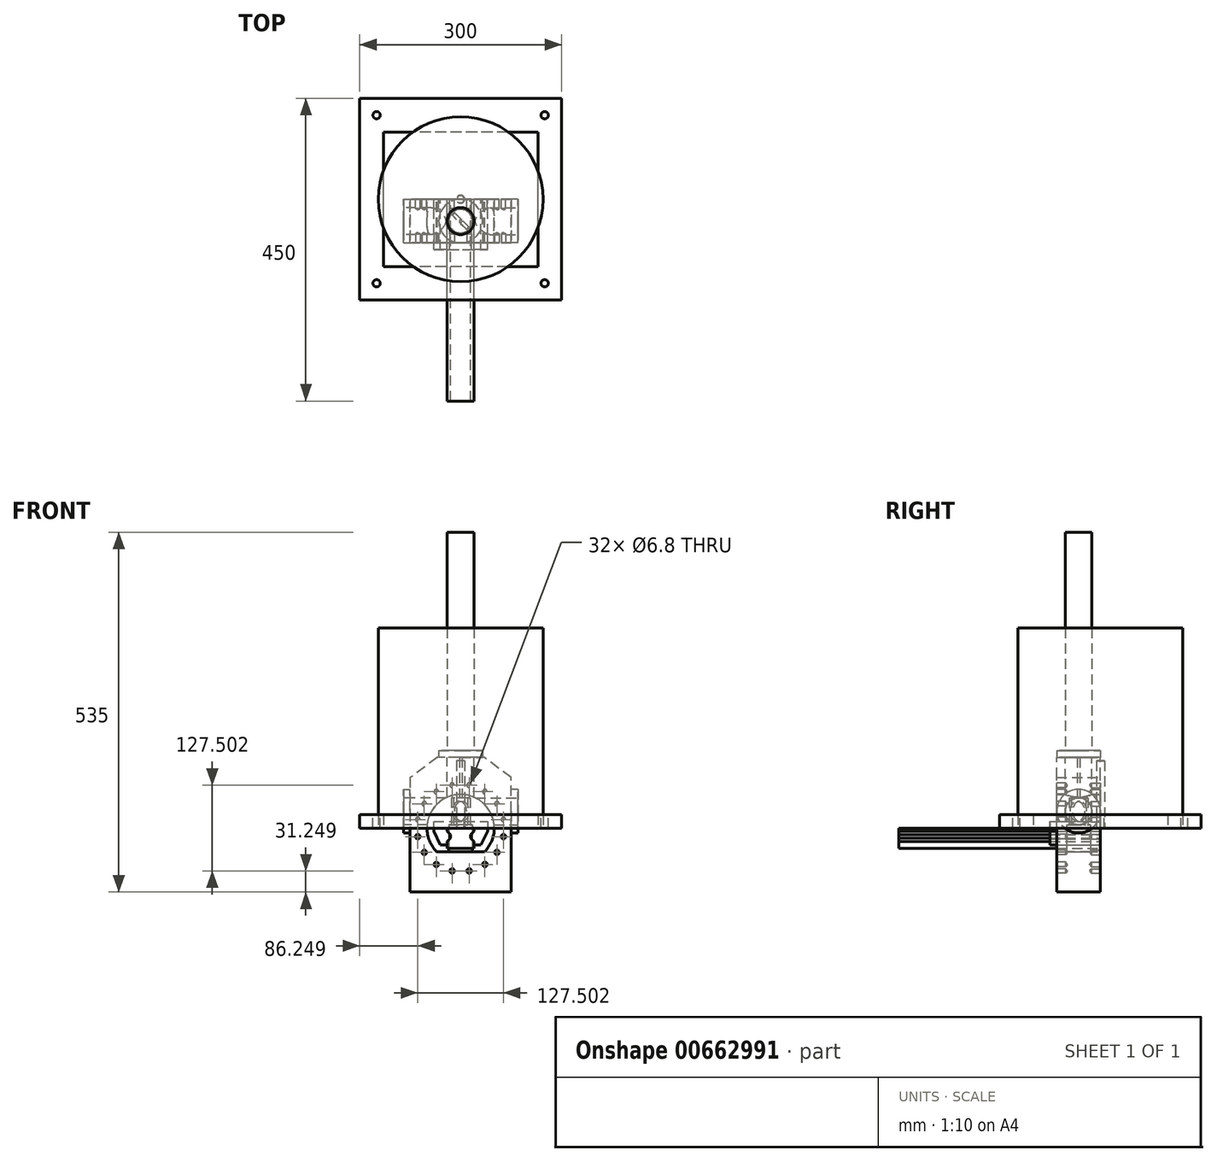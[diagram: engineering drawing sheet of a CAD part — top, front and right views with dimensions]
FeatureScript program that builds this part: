
annotation { "Feature Type Name" : "Feature", "Feature Type Description" : "" }
export const myFeature = defineFeature(function(context is Context, id is Id, definition is map)
    precondition{}
    {
        {
            var Q0;
            Q0=qCreatedBy(makeId("Front.planeOp"),FACE);
            var sketch = newSketch(context, id + "F0", { "sketchPlane" : qUnion([Q0])});
            skLineSegment(sketch, "E0", {"start": v(-75, -95) * mm, "end": v(75, -95) * mm});
            skLineSegment(sketch, "E1", {"start": v(75, -95) * mm, "end": v(75, 75) * mm});
            skLineSegment(sketch, "E2", {"start": v(75, 75) * mm, "end": v(35, 105) * mm});
            skLineSegment(sketch, "E3", {"start": v(35, 105) * mm, "end": v(-35, 105) * mm});
            skLineSegment(sketch, "E4", {"start": v(-35, 105) * mm, "end": v(-75, 75) * mm});
            skLineSegment(sketch, "E5", {"start": v(-75, 75) * mm, "end": v(-75, -95) * mm});
            skSolve(sketch);
        }
        {
            var Q0;
            Q0=makeQuery(id+"F0.imprint","IMPRINT",FACE,{"disambiguationData":[TD([[makeQuery(id+"F0.imprint","IMPRINT",EDGE,{"derivedFrom":sQuery(id+"F0.wireOp",EDGE,"E0")}),1.0]])]});
            extrude(context, id + "F1", {"entities" : qUnion([Q0]), "depth" : 65 * mm, "offsetDistance" : 25 * mm});
        }
        {
            var Q0;
            Q0=makeQuery(id+"F1.opExtrude","CAP_FACE",FACE,{"disambiguationData":[OSD([sQuery(id+"F0.wireOp",EDGE,"E0"),sQuery(id+"F0.wireOp",EDGE,"E1"),sQuery(id+"F0.wireOp",EDGE,"E2"),sQuery(id+"F0.wireOp",EDGE,"E3"),sQuery(id+"F0.wireOp",EDGE,"E4"),sQuery(id+"F0.wireOp",EDGE,"E5")])],"isStart":true});
            var sketch = newSketch(context, id + "F2", { "sketchPlane" : qUnion([Q0])});
            skArc(sketch, "E6", {"start": v(35.7, -35) * mm, "mid": v(0, 50) * mm, "end": v(-35.7, -35) * mm});
            skCircle(sketch, "E7", {"center": v(0, 0) * mm, "radius": 65 * mm, "construction": true});
            skLineSegment(sketch, "E8", {"start": v(-35.7, -35) * mm, "end": v(35.7, -35) * mm});
            skPoint(sketch, "E9", {"position": v(12.68, 63.75) * mm});
            skLineSegment(sketch, "E10", {"start": v(12.68, 63.75) * mm, "end": v(0, 0) * mm, "construction": true});
            skPoint(sketch, "E11.1.0", {"position": v(36.11, 54.05) * mm});
            skPoint(sketch, "E11.2.0", {"position": v(54.05, 36.11) * mm});
            skPoint(sketch, "E11.3.0", {"position": v(63.75, 12.68) * mm});
            skPoint(sketch, "E11.4.0", {"position": v(63.75, -12.68) * mm});
            skPoint(sketch, "E11.5.0", {"position": v(54.05, -36.11) * mm});
            skPoint(sketch, "E11.6.0", {"position": v(36.11, -54.05) * mm});
            skPoint(sketch, "E11.7.0", {"position": v(12.68, -63.75) * mm});
            skPoint(sketch, "E11.8.0", {"position": v(-12.68, -63.75) * mm});
            skPoint(sketch, "E11.9.0", {"position": v(-36.11, -54.05) * mm});
            skPoint(sketch, "E11.10.0", {"position": v(-54.05, -36.11) * mm});
            skPoint(sketch, "E11.11.0", {"position": v(-63.75, -12.68) * mm});
            skPoint(sketch, "E11.12.0", {"position": v(-63.75, 12.68) * mm});
            skPoint(sketch, "E11.13.0", {"position": v(-54.05, 36.11) * mm});
            skPoint(sketch, "E11.14.0", {"position": v(-36.11, 54.05) * mm});
            skPoint(sketch, "E11.15.0", {"position": v(-12.68, 63.75) * mm});
            skSolve(sketch);
        }
        {
            var Q0;
            Q0=makeQuery(id+"F2.imprint","IMPRINT",FACE,{"disambiguationData":[TD([[makeQuery(id+"F2.imprint","IMPRINT",EDGE,{"derivedFrom":sQuery(id+"F2.wireOp",EDGE,"E6")}),1.0]])]});
            extrude(context, id + "F3", {"entities" : qUnion([Q0]), "operationType" : NewBodyOperationType.REMOVE, "endBound" : BoundingType.THROUGH_ALL, "oppositeDirection" : true, "depth" : 25 * mm, "offsetDistance" : 25 * mm});
        }
        {
            var Q0;
            Q0=sQuery(id+"F2.wireOp",VERTEX,"E9");
            var Q1;
            Q1=sQuery(id+"F2.wireOp",VERTEX,"E11.1.0");
            var Q2;
            Q2=sQuery(id+"F2.wireOp",VERTEX,"E11.2.0");
            var Q3;
            Q3=sQuery(id+"F2.wireOp",VERTEX,"E11.3.0");
            var Q4;
            Q4=sQuery(id+"F2.wireOp",VERTEX,"E11.4.0");
            var Q5;
            Q5=sQuery(id+"F2.wireOp",VERTEX,"E11.5.0");
            var Q6;
            Q6=sQuery(id+"F2.wireOp",VERTEX,"E11.6.0");
            var Q7;
            Q7=sQuery(id+"F2.wireOp",VERTEX,"E11.7.0");
            var Q8;
            Q8=sQuery(id+"F2.wireOp",VERTEX,"E11.8.0");
            var Q9;
            Q9=sQuery(id+"F2.wireOp",VERTEX,"E11.9.0");
            var Q10;
            Q10=sQuery(id+"F2.wireOp",VERTEX,"E11.10.0");
            var Q11;
            Q11=sQuery(id+"F2.wireOp",VERTEX,"E11.11.0");
            var Q12;
            Q12=sQuery(id+"F2.wireOp",VERTEX,"E11.12.0");
            var Q13;
            Q13=sQuery(id+"F2.wireOp",VERTEX,"E11.13.0");
            var Q14;
            Q14=sQuery(id+"F2.wireOp",VERTEX,"E11.14.0");
            var Q15;
            Q15=sQuery(id+"F2.wireOp",VERTEX,"E11.15.0");
            var Q16;
            Q16=makeQuery(id+"F1.opExtrude","SWEPT_BODY",BODY,{"disambiguationData":[OSD([sQuery(id+"F0.wireOp",EDGE,"E0"),sQuery(id+"F0.wireOp",EDGE,"E1"),sQuery(id+"F0.wireOp",EDGE,"E2"),sQuery(id+"F0.wireOp",EDGE,"E3"),sQuery(id+"F0.wireOp",EDGE,"E4"),sQuery(id+"F0.wireOp",EDGE,"E5")])]});
            hole(context, id + "F4", {"style" : HoleStyle.SIMPLE, "endStyle" : HoleEndStyle.BLIND, "standardTappedOrClearance" : lookupTablePath({ "standard" : "ISO", "engagement" : "75%", "pitch" : "1.25 mm", "size" : "M8", "type" : "Tapped" }), "standardBlindInLast" : lookupTablePath({ "standard" : "ISO", "fit" : "Normal", "engagement" : "75%", "pitch" : "1.25 mm", "size" : "M8", "type" : "Clearance & tapped" }), "holeDiameter" : 6.8 * mm, "majorDiameter" : 8 * mm, "showTappedDepth" : true, "holeDepth" : 13.75 * mm, "isTappedThrough" : true, "tappedDepth" : 10 * mm, "tapClearance" : 3, "locations" : qUnion([Q0, Q1, Q2, Q3, Q4, Q5, Q6, Q7, Q8, Q9, Q10, Q11, Q12, Q13, Q14, Q15]), "scope" : qUnion([Q16])});
        }
        {
            var Q0;
            Q0=makeQuery(id+"F1.opExtrude","SWEPT_FACE",FACE,{"disambiguationData":[OSD([sQuery(id+"F0.wireOp",EDGE,"E3")])]});
            var sketch = newSketch(context, id + "F5", { "sketchPlane" : qUnion([Q0])});
            skCircle(sketch, "E12", {"center": v(0, -32.5) * mm, "radius": 32.5 * mm});
            skPoint(sketch, "E12.centerSnap0", {"position": v(0, -65) * mm});
            skPoint(sketch, "E12.centerSnap1", {"position": v(35, -32.5) * mm});
            skCircle(sketch, "E13", {"center": v(0, -32.5) * mm, "radius": 20 * mm});
            skSolve(sketch);
        }
        {
            var Q0;
            Q0=makeQuery(id+"F5.imprint","IMPRINT",FACE,{"disambiguationData":[TD([[makeQuery(id+"F5.imprint","IMPRINT",EDGE,{"derivedFrom":sQuery(id+"F5.wireOp",EDGE,"E13")}),-1.0]])]});
            var Q1;
            Q1=makeQuery(id+"F5.imprint","IMPRINT",FACE,{"disambiguationData":[TD([[makeQuery(id+"F5.imprint","IMPRINT",EDGE,{"derivedFrom":sQuery(id+"F5.wireOp",EDGE,"E13")}),1.0]])]});
            extrude(context, id + "F6", {"entities" : qUnion([Q0, Q1]), "operationType" : NewBodyOperationType.ADD, "depth" : 10 * mm, "offsetDistance" : 25 * mm});
        }
        {
            var Q0;
            Q0=makeQuery(id+"F5.imprint","IMPRINT",FACE,{"disambiguationData":[TD([[makeQuery(id+"F5.imprint","IMPRINT",EDGE,{"derivedFrom":sQuery(id+"F5.wireOp",EDGE,"E13")}),1.0]])]});
            var Q1;
            Q1=makeQuery(id+"F3.boolean.opBoolean","COPY",FACE,{"derivedFrom":makeQuery(id+"F3.opExtrude","SWEPT_FACE",FACE,{"disambiguationData":[OSD([sQuery(id+"F2.wireOp",EDGE,"E6")])]})});
            extrude(context, id + "F7", {"entities" : qUnion([Q0]), "operationType" : NewBodyOperationType.REMOVE, "endBound" : BoundingType.UP_TO_SURFACE, "oppositeDirection" : true, "depth" : 25 * mm, "endBoundEntityFace" : qUnion([Q1]), "offsetDistance" : 25 * mm});
        }
        {
            var Q0;
            Q0=makeQuery(id+"F6.opExtrude","CAP_FACE",FACE,{"disambiguationData":[OSD([sQuery(id+"F5.wireOp",EDGE,"E12")])],"isStart":false});
            var sketch = newSketch(context, id + "F8", { "sketchPlane" : qUnion([Q0])});
            skCircle(sketch, "E14", {"center": v(0, -32.5) * mm, "radius": 20 * mm});
            skSolve(sketch);
        }
        {
            var Q0;
            Q0=makeQuery(id+"F8.imprint","IMPRINT",FACE,{"disambiguationData":[TD([[makeQuery(id+"F8.imprint","IMPRINT",EDGE,{"derivedFrom":sQuery(id+"F8.wireOp",EDGE,"E14")}),1.0]])]});
            extrude(context, id + "F9", {"entities" : qUnion([Q0]), "operationType" : NewBodyOperationType.ADD, "depth" : 325 * mm, "offsetDistance" : 25 * mm});
        }
        {
            var Q0;
            Q0=makeQuery(id+"F1.opExtrude","CAP_FACE",FACE,{"disambiguationData":[OSD([sQuery(id+"F0.wireOp",EDGE,"E0"),sQuery(id+"F0.wireOp",EDGE,"E1"),sQuery(id+"F0.wireOp",EDGE,"E2"),sQuery(id+"F0.wireOp",EDGE,"E3"),sQuery(id+"F0.wireOp",EDGE,"E4"),sQuery(id+"F0.wireOp",EDGE,"E5")])],"isStart":false});
            var sketch = newSketch(context, id + "F10", { "sketchPlane" : qUnion([Q0])});
            skCircle(sketch, "E15", {"center": v(0, 0) * mm, "radius": 65 * mm, "construction": true});
            skPoint(sketch, "E16", {"position": v(12.68, 63.75) * mm});
            skLineSegment(sketch, "E17", {"start": v(12.68, 63.75) * mm, "end": v(0, 0) * mm, "construction": true});
            skPoint(sketch, "E18.1.0", {"position": v(-12.68, 63.75) * mm});
            skPoint(sketch, "E18.2.0", {"position": v(-36.11, 54.05) * mm});
            skPoint(sketch, "E18.3.0", {"position": v(-54.05, 36.11) * mm});
            skPoint(sketch, "E18.4.0", {"position": v(-63.75, 12.68) * mm});
            skPoint(sketch, "E18.5.0", {"position": v(-63.75, -12.68) * mm});
            skPoint(sketch, "E18.6.0", {"position": v(-54.05, -36.11) * mm});
            skPoint(sketch, "E18.7.0", {"position": v(-36.11, -54.05) * mm});
            skPoint(sketch, "E18.8.0", {"position": v(-12.68, -63.75) * mm});
            skPoint(sketch, "E18.9.0", {"position": v(12.68, -63.75) * mm});
            skPoint(sketch, "E18.10.0", {"position": v(36.11, -54.05) * mm});
            skPoint(sketch, "E18.11.0", {"position": v(54.05, -36.11) * mm});
            skPoint(sketch, "E18.12.0", {"position": v(63.75, -12.68) * mm});
            skPoint(sketch, "E18.13.0", {"position": v(63.75, 12.68) * mm});
            skPoint(sketch, "E18.14.0", {"position": v(54.05, 36.11) * mm});
            skPoint(sketch, "E18.15.0", {"position": v(36.11, 54.05) * mm});
            skSolve(sketch);
        }
        {
            var Q0;
            Q0=sQuery(id+"F10.wireOp",VERTEX,"E16");
            var Q1;
            Q1=sQuery(id+"F10.wireOp",VERTEX,"E18.15.0");
            var Q2;
            Q2=sQuery(id+"F10.wireOp",VERTEX,"E18.14.0");
            var Q3;
            Q3=sQuery(id+"F10.wireOp",VERTEX,"E18.13.0");
            var Q4;
            Q4=sQuery(id+"F10.wireOp",VERTEX,"E18.12.0");
            var Q5;
            Q5=sQuery(id+"F10.wireOp",VERTEX,"E18.11.0");
            var Q6;
            Q6=sQuery(id+"F10.wireOp",VERTEX,"E18.10.0");
            var Q7;
            Q7=sQuery(id+"F10.wireOp",VERTEX,"E18.9.0");
            var Q8;
            Q8=sQuery(id+"F10.wireOp",VERTEX,"E18.8.0");
            var Q9;
            Q9=sQuery(id+"F10.wireOp",VERTEX,"E18.7.0");
            var Q10;
            Q10=sQuery(id+"F10.wireOp",VERTEX,"E18.6.0");
            var Q11;
            Q11=sQuery(id+"F10.wireOp",VERTEX,"E18.5.0");
            var Q12;
            Q12=sQuery(id+"F10.wireOp",VERTEX,"E18.4.0");
            var Q13;
            Q13=sQuery(id+"F10.wireOp",VERTEX,"E18.3.0");
            var Q14;
            Q14=sQuery(id+"F10.wireOp",VERTEX,"E18.2.0");
            var Q15;
            Q15=sQuery(id+"F10.wireOp",VERTEX,"E18.1.0");
            var Q16;
            Q16=makeQuery(id+"F1.opExtrude","SWEPT_BODY",BODY,{"disambiguationData":[OSD([sQuery(id+"F0.wireOp",EDGE,"E0"),sQuery(id+"F0.wireOp",EDGE,"E1"),sQuery(id+"F0.wireOp",EDGE,"E2"),sQuery(id+"F0.wireOp",EDGE,"E3"),sQuery(id+"F0.wireOp",EDGE,"E4"),sQuery(id+"F0.wireOp",EDGE,"E5")])]});
            hole(context, id + "F11", {"style" : HoleStyle.SIMPLE, "endStyle" : HoleEndStyle.BLIND, "standardTappedOrClearance" : lookupTablePath({ "standard" : "ISO", "engagement" : "75%", "pitch" : "1.25 mm", "size" : "M8", "type" : "Tapped" }), "standardBlindInLast" : lookupTablePath({ "fit" : "Normal", "standard" : "ISO", "engagement" : "75%", "pitch" : "1.25 mm", "size" : "M8", "type" : "Clearance & tapped" }), "holeDiameter" : 6.8 * mm, "majorDiameter" : 8 * mm, "showTappedDepth" : true, "holeDepth" : 13.75 * mm, "isTappedThrough" : true, "tappedDepth" : 10 * mm, "tapClearance" : 3, "locations" : qUnion([Q0, Q1, Q2, Q3, Q4, Q5, Q6, Q7, Q8, Q9, Q10, Q11, Q12, Q13, Q14, Q15]), "scope" : qUnion([Q16])});
        }
        {
            var Q0;
            Q0=makeQuery(id+"F1.opExtrude","SWEPT_FACE",FACE,{"disambiguationData":[OSD([sQuery(id+"F0.wireOp",EDGE,"E5")])]});
            var sketch = newSketch(context, id + "F12", { "sketchPlane" : qUnion([Q0])});
            skCircle(sketch, "E19", {"center": v(32.5, 25) * mm, "radius": 20 * mm});
            skPoint(sketch, "E19.centerSnap0", {"position": v(32.5, 75) * mm});
            skCircle(sketch, "E20", {"center": v(32.5, 25) * mm, "radius": 32.5 * mm});
            skSolve(sketch);
        }
        {
            var Q0;
            Q0=makeQuery(id+"F12.imprint","IMPRINT",FACE,{"disambiguationData":[TD([[makeQuery(id+"F12.imprint","IMPRINT",EDGE,{"derivedFrom":sQuery(id+"F12.wireOp",EDGE,"E19")}),1.0]])]});
            var Q1;
            Q1=makeQuery(id+"F3.boolean.opBoolean","COPY",FACE,{"derivedFrom":makeQuery(id+"F3.opExtrude","SWEPT_FACE",FACE,{"disambiguationData":[OSD([sQuery(id+"F2.wireOp",EDGE,"E6")])]})});
            extrude(context, id + "F13", {"entities" : qUnion([Q0]), "operationType" : NewBodyOperationType.REMOVE, "endBound" : BoundingType.UP_TO_SURFACE, "oppositeDirection" : true, "depth" : 25 * mm, "endBoundEntityFace" : qUnion([Q1]), "offsetDistance" : 25 * mm});
        }
        {
            var Q0;
            Q0=makeQuery(id+"F12.imprint","IMPRINT",FACE,{"disambiguationData":[TD([[makeQuery(id+"F12.imprint","IMPRINT",EDGE,{"derivedFrom":sQuery(id+"F12.wireOp",EDGE,"E19")}),-1.0]])]});
            extrude(context, id + "F14", {"entities" : qUnion([Q0]), "operationType" : NewBodyOperationType.ADD, "depth" : 10 * mm, "offsetDistance" : 25 * mm});
        }
        {
            var Q0;
            Q0=makeQuery(id+"F1.opExtrude","SWEPT_FACE",FACE,{"disambiguationData":[OSD([sQuery(id+"F0.wireOp",EDGE,"E1")])]});
            var sketch = newSketch(context, id + "F15", { "sketchPlane" : qUnion([Q0])});
            skCircle(sketch, "E21", {"center": v(-32.5, 25) * mm, "radius": 20 * mm});
            skPoint(sketch, "E21.centerSnap0", {"position": v(-32.5, 75) * mm});
            skCircle(sketch, "E22", {"center": v(-32.5, 25) * mm, "radius": 32.5 * mm});
            skSolve(sketch);
        }
        {
            var Q0;
            Q0=makeQuery(id+"F15.imprint","IMPRINT",FACE,{"disambiguationData":[TD([[makeQuery(id+"F15.imprint","IMPRINT",EDGE,{"derivedFrom":sQuery(id+"F15.wireOp",EDGE,"E21")}),1.0]])]});
            var Q1;
            Q1=makeQuery(id+"F3.boolean.opBoolean","COPY",FACE,{"derivedFrom":makeQuery(id+"F3.opExtrude","SWEPT_FACE",FACE,{"disambiguationData":[OSD([sQuery(id+"F2.wireOp",EDGE,"E6")])]})});
            extrude(context, id + "F16", {"entities" : qUnion([Q0]), "operationType" : NewBodyOperationType.REMOVE, "endBound" : BoundingType.UP_TO_SURFACE, "oppositeDirection" : true, "depth" : 25 * mm, "endBoundEntityFace" : qUnion([Q1]), "offsetDistance" : 25 * mm});
        }
        {
            var Q0;
            Q0=makeQuery(id+"F15.imprint","IMPRINT",FACE,{"disambiguationData":[TD([[makeQuery(id+"F15.imprint","IMPRINT",EDGE,{"derivedFrom":sQuery(id+"F15.wireOp",EDGE,"E21")}),-1.0]])]});
            extrude(context, id + "F17", {"entities" : qUnion([Q0]), "operationType" : NewBodyOperationType.ADD, "depth" : 10 * mm, "offsetDistance" : 25 * mm});
        }
        {
            var Q0;
            Q0=makeQuery(id+"F3.boolean.opBoolean","COPY",FACE,{"derivedFrom":makeQuery(id+"F3.opExtrude","SWEPT_FACE",FACE,{"disambiguationData":[OSD([sQuery(id+"F2.wireOp",EDGE,"E8")])]})});
            var sketch = newSketch(context, id + "F18", { "sketchPlane" : qUnion([Q0])});
            skCircle(sketch, "E23", {"center": v(0, -32.5) * mm, "radius": 17.5 * mm});
            skPoint(sketch, "E23.centerSnap0", {"position": v(35.7, -32.5) * mm});
            skSolve(sketch);
        }
        {
            var Q0;
            Q0=makeQuery(id+"F18.imprint","IMPRINT",FACE,{"disambiguationData":[TD([[makeQuery(id+"F18.imprint","IMPRINT",EDGE,{"derivedFrom":sQuery(id+"F18.wireOp",EDGE,"E23")}),1.0]])]});
            extrude(context, id + "F19", {"entities" : qUnion([Q0]), "operationType" : NewBodyOperationType.ADD, "depth" : 40 * mm, "offsetDistance" : 25 * mm});
        }
        {
            var Q0;
            Q0=makeQuery(id+"F19.opExtrude","CAP_FACE",FACE,{"disambiguationData":[OSD([sQuery(id+"F18.wireOp",EDGE,"E23")])],"isStart":false});
            var sketch = newSketch(context, id + "F20", { "sketchPlane" : qUnion([Q0])});
            skLineSegment(sketch, "E24", {"start": v(14.02, -42.98) * mm, "end": v(-10.48, -18.48) * mm});
            skLineSegment(sketch, "E25", {"start": v(0, -32.5) * mm, "end": v(12.37, -44.87) * mm, "construction": true});
            skLineSegment(sketch, "E26", {"start": v(10.48, -46.52) * mm, "end": v(-14.02, -22.02) * mm});
            skSolve(sketch);
        }
        {
            var Q0;
            {var subQ0=sQuery(id+"F20.wireOp",EDGE,"E24");Q0=makeQuery(id+"F20.imprint","IMPRINT",FACE,{"disambiguationData":[TD([[makeQuery(id+"F20.imprint","IMPRINT",EDGE,{"derivedFrom":subQ0}),1.0]])]});}
            extrude(context, id + "F21", {"entities" : qUnion([Q0]), "operationType" : NewBodyOperationType.ADD, "depth" : 40 * mm, "offsetDistance" : 25 * mm});
        }
        {
            var Q0;
            Q0=makeQuery(id+"F21.opExtrude","SWEPT_FACE",FACE,{"disambiguationData":[OSD([sQuery(id+"F20.wireOp",EDGE,"E24")])]});
            var sketch = newSketch(context, id + "F22", { "sketchPlane" : qUnion([Q0])});
            skCircle(sketch, "E27", {"center": v(-22.98, 25) * mm, "radius": 15 * mm});
            skPoint(sketch, "E27.centerSnap0", {"position": v(-22.98, 45) * mm});
            skSolve(sketch);
        }
        {
            var Q0;
            Q0=makeQuery(id+"F22.imprint","IMPRINT",FACE,{"disambiguationData":[TD([[makeQuery(id+"F22.imprint","IMPRINT",EDGE,{"derivedFrom":sQuery(id+"F22.wireOp",EDGE,"E27")}),1.0]])]});
            var Q1;
            Q1=makeQuery(id+"F21.opExtrude","SWEPT_FACE",FACE,{"disambiguationData":[OSD([sQuery(id+"F20.wireOp",EDGE,"E26")])]});
            extrude(context, id + "F23", {"entities" : qUnion([Q0]), "operationType" : NewBodyOperationType.REMOVE, "endBound" : BoundingType.UP_TO_SURFACE, "oppositeDirection" : true, "depth" : 25 * mm, "endBoundEntityFace" : qUnion([Q1]), "offsetDistance" : 25 * mm});
        }
        {
            var Q0;
            Q0=makeQuery(id+"F21.opExtrude","CAP_FACE",FACE,{"disambiguationData":[OSD([sQuery(id+"F18.wireOp",EDGE,"E23"),sQuery(id+"F20.wireOp",EDGE,"E24"),sQuery(id+"F20.wireOp",EDGE,"E26")])],"isStart":false});
            var sketch = newSketch(context, id + "F24", { "sketchPlane" : qUnion([Q0])});
            skCircle(sketch, "E28", {"center": v(0, -32.5) * mm, "radius": 2 * mm});
            skSolve(sketch);
        }
        {
            var Q0;
            Q0=makeQuery(id+"F24.imprint","IMPRINT",FACE,{"disambiguationData":[TD([[makeQuery(id+"F24.imprint","IMPRINT",EDGE,{"derivedFrom":sQuery(id+"F24.wireOp",EDGE,"E28")}),1.0]])]});
            extrude(context, id + "F25", {"entities" : qUnion([Q0]), "operationType" : NewBodyOperationType.ADD, "endBound" : BoundingType.UP_TO_NEXT, "depth" : 25 * mm, "offsetDistance" : 25 * mm});
        }
        {
            var Q0;
            Q0=qCreatedBy(makeId("Top.planeOp"),FACE);
            var sketch = newSketch(context, id + "F26", { "sketchPlane" : qUnion([Q0])});
            skLineSegment(sketch, "E29.bottom", {"start": v(-150, 150) * mm, "end": v(150, 150) * mm});
            skLineSegment(sketch, "E29.top", {"start": v(-150, -150) * mm, "end": v(150, -150) * mm});
            skLineSegment(sketch, "E29.left", {"start": v(-150, 150) * mm, "end": v(-150, -150) * mm});
            skLineSegment(sketch, "E29.right", {"start": v(150, 150) * mm, "end": v(150, -150) * mm});
            skPoint(sketch, "E29.middle", {"position": v(0, 0) * mm});
            skSolve(sketch);
        }
        {
            var Q0;
            Q0=makeQuery(id+"F26.imprint","IMPRINT",FACE,{"disambiguationData":[TD([[makeQuery(id+"F26.imprint","IMPRINT",EDGE,{"derivedFrom":sQuery(id+"F26.wireOp",EDGE,"E29.bottom")}),-1.0]])]});
            extrude(context, id + "F27", {"entities" : qUnion([Q0]), "depth" : 20 * mm, "offsetDistance" : 25 * mm});
        }
        {
            var Q0;
            Q0=makeQuery(id+"F27.opExtrude","CAP_FACE",FACE,{"disambiguationData":[OSD([sQuery(id+"F26.wireOp",EDGE,"E29.bottom"),sQuery(id+"F26.wireOp",EDGE,"E29.top"),sQuery(id+"F26.wireOp",EDGE,"E29.left"),sQuery(id+"F26.wireOp",EDGE,"E29.right")])],"isStart":false});
            var sketch = newSketch(context, id + "F28", { "sketchPlane" : qUnion([Q0])});
            skCircle(sketch, "E30", {"center": v(0, 0) * mm, "radius": 122.5 * mm, "construction": true});
            skLineSegment(sketch, "E31.bottom", {"start": v(-125, -125) * mm, "end": v(125, -125) * mm, "construction": true});
            skLineSegment(sketch, "E31.top", {"start": v(-125, 125) * mm, "end": v(125, 125) * mm, "construction": true});
            skLineSegment(sketch, "E31.left", {"start": v(-125, -125) * mm, "end": v(-125, 125) * mm, "construction": true});
            skLineSegment(sketch, "E31.right", {"start": v(125, -125) * mm, "end": v(125, 125) * mm, "construction": true});
            skSolve(sketch);
        }
        {
            var Q0;
            Q0=sQuery(id+"F28.wireOp",VERTEX,"E31.bottom.end");
            var Q1;
            Q1=sQuery(id+"F28.wireOp",VERTEX,"E31.top.end");
            var Q2;
            Q2=sQuery(id+"F28.wireOp",VERTEX,"E31.top.start");
            var Q3;
            Q3=sQuery(id+"F28.wireOp",VERTEX,"E31.bottom.start");
            var Q4;
            Q4=sQuery(id+"F28.wireOp",VERTEX,"E30.center");
            var Q5;
            Q5=makeQuery(id+"F27.opExtrude","SWEPT_BODY",BODY,{"disambiguationData":[OSD([sQuery(id+"F26.wireOp",EDGE,"E29.bottom"),sQuery(id+"F26.wireOp",EDGE,"E29.top"),sQuery(id+"F26.wireOp",EDGE,"E29.left"),sQuery(id+"F26.wireOp",EDGE,"E29.right")])]});
            hole(context, id + "F29", {"style" : HoleStyle.SIMPLE, "endStyle" : HoleEndStyle.THROUGH, "standardTappedOrClearance" : lookupTablePath({ "standard" : "ISO", "engagement" : "75%", "pitch" : "1.25 mm", "size" : "M12", "type" : "Tapped" }), "standardBlindInLast" : lookupTablePath({ "standard" : "ISO", "fit" : "Normal", "engagement" : "75%", "pitch" : "1.25 mm", "size" : "M12", "type" : "Clearance & tapped" }), "holeDiameter" : 10.8 * mm, "majorDiameter" : 12 * mm, "showTappedDepth" : true, "isTappedThrough" : true, "tappedDepth" : 10 * mm, "tapClearance" : 3, "locations" : qUnion([Q0, Q1, Q2, Q3, Q4]), "scope" : qUnion([Q5])});
        }
        {
            var Q0;
            Q0=qCreatedBy(makeId("Top.planeOp"),FACE);
            var sketch = newSketch(context, id + "F30", { "sketchPlane" : qUnion([Q0])});
            skLineSegment(sketch, "E32.bottom", {"start": v(-150, -150) * mm, "end": v(150, -150) * mm});
            skLineSegment(sketch, "E32.top", {"start": v(-150, 150) * mm, "end": v(150, 150) * mm});
            skLineSegment(sketch, "E32.left", {"start": v(-150, -150) * mm, "end": v(-150, 150) * mm});
            skLineSegment(sketch, "E32.right", {"start": v(150, -150) * mm, "end": v(150, 150) * mm});
            skPoint(sketch, "E32.middle", {"position": v(0, 0) * mm});
            skSolve(sketch);
        }
        {
            var Q0;
            Q0=makeQuery(id+"F30.imprint","IMPRINT",FACE,{"disambiguationData":[TD([[makeQuery(id+"F30.imprint","IMPRINT",EDGE,{"derivedFrom":sQuery(id+"F30.wireOp",EDGE,"E32.bottom")}),1.0]])]});
            extrude(context, id + "F31", {"entities" : qUnion([Q0]), "depth" : 20 * mm, "offsetDistance" : 25 * mm});
        }
        {
            var Q0;
            Q0=makeQuery(id+"F31.opExtrude","CAP_FACE",FACE,{"disambiguationData":[OSD([sQuery(id+"F30.wireOp",EDGE,"E32.bottom"),sQuery(id+"F30.wireOp",EDGE,"E32.top"),sQuery(id+"F30.wireOp",EDGE,"E32.left"),sQuery(id+"F30.wireOp",EDGE,"E32.right")])],"isStart":false});
            var sketch = newSketch(context, id + "F32", { "sketchPlane" : qUnion([Q0])});
            skLineSegment(sketch, "E33.bottom", {"start": v(125, -125) * mm, "end": v(-125, -125) * mm, "construction": true});
            skLineSegment(sketch, "E33.top", {"start": v(125, 125) * mm, "end": v(-125, 125) * mm, "construction": true});
            skLineSegment(sketch, "E33.left", {"start": v(125, -125) * mm, "end": v(125, 125) * mm, "construction": true});
            skLineSegment(sketch, "E33.right", {"start": v(-125, -125) * mm, "end": v(-125, 125) * mm, "construction": true});
            skPoint(sketch, "E33.middle", {"position": v(0, 0) * mm});
            skSolve(sketch);
        }
        {
            var Q0;
            Q0=sQuery(id+"F32.wireOp",VERTEX,"E33.middle");
            var Q1;
            Q1=sQuery(id+"F32.wireOp",VERTEX,"E33.top.end");
            var Q2;
            Q2=sQuery(id+"F32.wireOp",VERTEX,"E33.bottom.end");
            var Q3;
            Q3=sQuery(id+"F32.wireOp",VERTEX,"E33.bottom.start");
            var Q4;
            Q4=sQuery(id+"F32.wireOp",VERTEX,"E33.top.start");
            var Q5;
            Q5=makeQuery(id+"F31.opExtrude","SWEPT_BODY",BODY,{"disambiguationData":[OSD([sQuery(id+"F30.wireOp",EDGE,"E32.bottom"),sQuery(id+"F30.wireOp",EDGE,"E32.top"),sQuery(id+"F30.wireOp",EDGE,"E32.left"),sQuery(id+"F30.wireOp",EDGE,"E32.right")])]});
            hole(context, id + "F33", {"style" : HoleStyle.SIMPLE, "endStyle" : HoleEndStyle.THROUGH, "standardTappedOrClearance" : lookupTablePath({ "standard" : "ISO", "engagement" : "75%", "pitch" : "1.25 mm", "size" : "M12", "type" : "Tapped" }), "standardBlindInLast" : lookupTablePath({ "fit" : "Normal", "standard" : "ISO", "engagement" : "75%", "pitch" : "1.25 mm", "size" : "M12", "type" : "Clearance & tapped" }), "holeDiameter" : 10.8 * mm, "majorDiameter" : 12 * mm, "showTappedDepth" : true, "isTappedThrough" : true, "tappedDepth" : 10 * mm, "tapClearance" : 3, "locations" : qUnion([Q0, Q1, Q2, Q3, Q4]), "scope" : qUnion([Q5])});
        }
        {
            var Q0;
            Q0=qCreatedBy(makeId("Front.planeOp"),FACE);
            var sketch = newSketch(context, id + "F34", { "sketchPlane" : qUnion([Q0])});
            skLineSegment(sketch, "E34", {"start": v(0, -30) * mm, "end": v(-20, -30) * mm});
            skLineSegment(sketch, "E35", {"start": v(-20, -30) * mm, "end": v(-20, -20) * mm});
            skLineSegment(sketch, "E36", {"start": v(-20, -20) * mm, "end": v(-15, -15) * mm});
            skLineSegment(sketch, "E37", {"start": v(-15, -15) * mm, "end": v(-15, -10) * mm});
            skLineSegment(sketch, "E38", {"start": v(-15, -10) * mm, "end": v(-20, -5) * mm});
            skLineSegment(sketch, "E39", {"start": v(-20, -5) * mm, "end": v(-20, 0) * mm});
            skLineSegment(sketch, "E40", {"start": v(-20, 0) * mm, "end": v(0, 0) * mm});
            skLineSegment(sketch, "E41", {"start": v(0, 0) * mm, "end": v(20, 0) * mm});
            skLineSegment(sketch, "E42", {"start": v(20, 0) * mm, "end": v(20, -5) * mm});
            skLineSegment(sketch, "E43", {"start": v(20, -5) * mm, "end": v(15, -10) * mm});
            skLineSegment(sketch, "E44", {"start": v(15, -10) * mm, "end": v(15, -15) * mm});
            skLineSegment(sketch, "E45", {"start": v(15, -15) * mm, "end": v(20, -20) * mm});
            skLineSegment(sketch, "E46", {"start": v(20, -20) * mm, "end": v(20, -30) * mm});
            skLineSegment(sketch, "E47", {"start": v(20, -30) * mm, "end": v(0, -30) * mm});
            skLineSegment(sketch, "E48", {"start": v(-40, 10) * mm, "end": v(0, 10) * mm});
            skLineSegment(sketch, "E49", {"start": v(40, 10) * mm, "end": v(40, -5) * mm});
            skLineSegment(sketch, "E50", {"start": v(40, -5) * mm, "end": v(30, -25) * mm});
            skLineSegment(sketch, "E51", {"start": v(30, -25) * mm, "end": v(20, -25) * mm});
            skLineSegment(sketch, "E52", {"start": v(-20, -25) * mm, "end": v(-30, -25) * mm});
            skLineSegment(sketch, "E53", {"start": v(-30, -25) * mm, "end": v(-40, -5) * mm});
            skLineSegment(sketch, "E54", {"start": v(-40, -5) * mm, "end": v(-40, 10) * mm});
            skLineSegment(sketch, "E55", {"start": v(0, 10) * mm, "end": v(40, 10) * mm});
            skLineSegment(sketch, "E56", {"start": v(-16, -16) * mm, "end": v(-16, -9) * mm});
            skLineSegment(sketch, "E57", {"start": v(16, -16) * mm, "end": v(16, -9) * mm});
            skSolve(sketch);
        }
        {
            var Q0;
            {var subQ7=sQuery(id+"F34.wireOp",EDGE,"E34");Q0=makeQuery(id+"F34.imprint","IMPRINT",FACE,{"disambiguationData":[TD([[makeQuery(id+"F34.imprint","IMPRINT",EDGE,{"derivedFrom":subQ7}),-1.0]])]});}
            extrude(context, id + "F35", {"entities" : qUnion([Q0]), "depth" : 300 * mm, "offsetDistance" : 25 * mm});
        }
        {
            var Q0;
            {var subQ11=sQuery(id+"F34.wireOp",EDGE,"E39");Q0=makeQuery(id+"F34.imprint","IMPRINT",FACE,{"disambiguationData":[TD([[makeQuery(id+"F34.imprint","IMPRINT",EDGE,{"derivedFrom":subQ11}),1.0]])]});}
            extrude(context, id + "F36", {"entities" : qUnion([Q0]), "depth" : 75 * mm, "offsetDistance" : 25 * mm});
        }
        {
            var Q0;
            Q0=qCreatedBy(makeId("Top.planeOp"),FACE);
            var sketch = newSketch(context, id + "F37", { "sketchPlane" : qUnion([Q0])});
            skCircle(sketch, "E58", {"center": v(0, 0) * mm, "radius": 6 * mm});
            skSolve(sketch);
        }
        {
            var Q0;
            Q0=makeQuery(id+"F37.imprint","IMPRINT",FACE,{"disambiguationData":[TD([[makeQuery(id+"F37.imprint","IMPRINT",EDGE,{"derivedFrom":sQuery(id+"F37.wireOp",EDGE,"E58")}),1.0]])]});
            extrude(context, id + "F38", {"entities" : qUnion([Q0]), "depth" : 100 * mm, "offsetDistance" : 25 * mm});
        }
        {
            var Q0;
            Q0=qCreatedBy(makeId("Top.planeOp"),FACE);
            var sketch = newSketch(context, id + "F39", { "sketchPlane" : qUnion([Q0])});
            skLineSegment(sketch, "E59.bottom", {"start": v(115, -100) * mm, "end": v(-115, -100) * mm});
            skLineSegment(sketch, "E59.top", {"start": v(115, 100) * mm, "end": v(-115, 100) * mm});
            skLineSegment(sketch, "E59.left", {"start": v(115, -100) * mm, "end": v(115, 100) * mm});
            skLineSegment(sketch, "E59.right", {"start": v(-115, -100) * mm, "end": v(-115, 100) * mm});
            skPoint(sketch, "E59.middle", {"position": v(0, 0) * mm});
            skSolve(sketch);
        }
        {
            var Q0;
            Q0=makeQuery(id+"F39.imprint","IMPRINT",FACE,{"disambiguationData":[TD([[makeQuery(id+"F39.imprint","IMPRINT",EDGE,{"derivedFrom":sQuery(id+"F39.wireOp",EDGE,"E59.bottom")}),-1.0]])]});
            extrude(context, id + "F40", {"entities" : qUnion([Q0]), "depth" : 20 * mm, "offsetDistance" : 25 * mm});
        }
        {
            var Q0;
            Q0=qCreatedBy(makeId("Top.planeOp"),FACE);
            var sketch = newSketch(context, id + "F41", { "sketchPlane" : qUnion([Q0])});
            skCircle(sketch, "E60", {"center": v(0, 0) * mm, "radius": 122.5 * mm});
            skSolve(sketch);
        }
        {
            var Q0;
            Q0=makeQuery(id+"F41.imprint","IMPRINT",FACE,{"disambiguationData":[TD([[makeQuery(id+"F41.imprint","IMPRINT",EDGE,{"derivedFrom":sQuery(id+"F41.wireOp",EDGE,"E60")}),1.0]])]});
            extrude(context, id + "F42", {"entities" : qUnion([Q0]), "depth" : 297.5 * mm, "offsetDistance" : 25 * mm});
        }
    });
